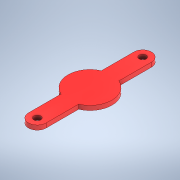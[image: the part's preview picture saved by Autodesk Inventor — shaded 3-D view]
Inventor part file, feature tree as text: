
AUTODESK INVENTOR PART (.ipt)
format: ipt  version: 2021 (Build 250183000, 183)  size: 120,832 bytes
history: native  units: mm
features: other x1, extrude x1, sketch x1
ambient origin geometry x8: Origin, YZ Plane, XZ Plane, XY Plane, X Axis, Y Axis, Z Axis, Center Point
bodies: Solid1 (feature_tree)
feature tree (3):
  other  "<userpath>\Documents\Semestre8\Robótica\Proyecto-Rob\Piezas\ParámetrosGripper.xlsx"
  extrude  "Extrusion1"  Depth=5.0mm
  sketch  "Sketch1"  dims[d0=50.0mm d1=8.0mm d2=8.0mm d3=20.0mm d4=120.0mm d5=5.0mm d6=0.0mm]
